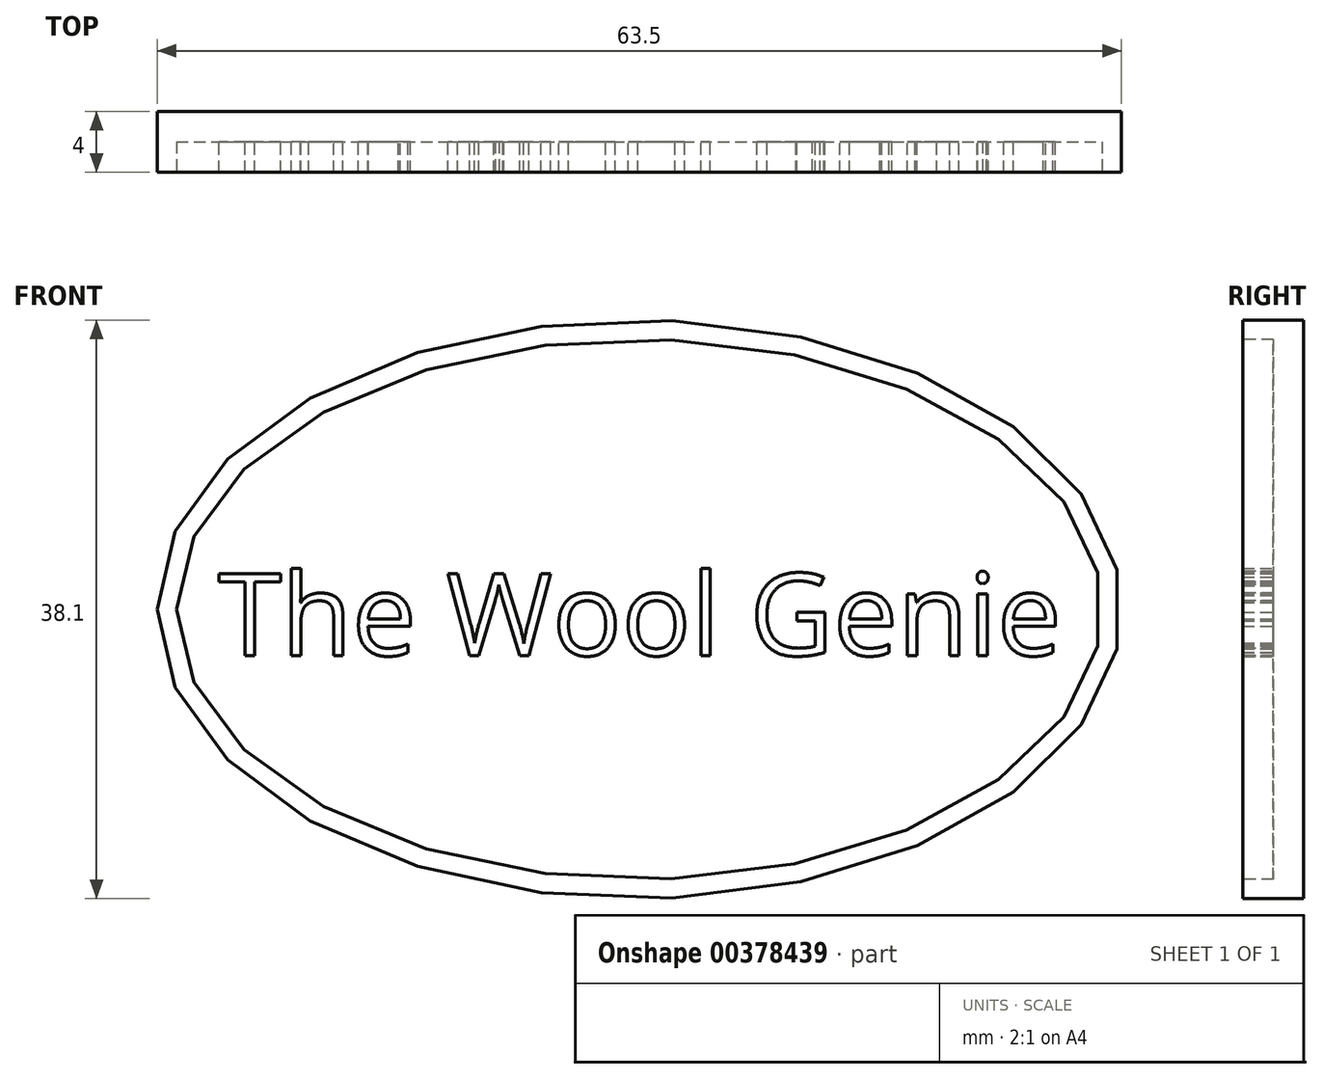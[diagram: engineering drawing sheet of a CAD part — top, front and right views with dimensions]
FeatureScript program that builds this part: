
annotation { "Feature Type Name" : "Feature", "Feature Type Description" : "" }
export const myFeature = defineFeature(function(context is Context, id is Id, definition is map)
    precondition{}
    {
        {
            var Q0;
            Q0=qCreatedBy(makeId("Front.planeOp"),FACE);
            var sketch = newSketch(context, id + "F0", { "sketchPlane" : qUnion([Q0])});
            skEllipse(sketch, "E0", {"center": v(0, 0) * mm, "majorRadius": 31.75 * mm, "minorRadius": 19.05 * mm, "majorAxis": v(-1, 0)});
            skSolve(sketch);
        }
        {
            var Q0;
            Q0=makeQuery(id+"F0.imprint","IMPRINT",FACE,{"disambiguationData":[TD([[makeQuery(id+"F0.imprint","IMPRINT",EDGE,{"derivedFrom":sQuery(id+"F0.wireOp",EDGE,"E0")}),1.0]])]});
            extrude(context, id + "F1", {"entities" : qUnion([Q0]), "depth" : 4 * mm});
        }
        {
            var Q0;
            Q0=makeQuery(id+"F1.opExtrude","CAP_FACE",FACE,{"disambiguationData":[OSD([sQuery(id+"F0.wireOp",EDGE,"E0")])],"isStart":false});
            var sketch = newSketch(context, id + "F2", { "sketchPlane" : qUnion([Q0])});
            skEllipse(sketch, "E1", {"center": v(0, 0) * mm, "majorRadius": 30.48 * mm, "minorRadius": 17.78 * mm, "majorAxis": v(-1, 0)});
            skSolve(sketch);
        }
        {
            var Q0;
            Q0=makeQuery(id+"F2.imprint","IMPRINT",FACE,{"disambiguationData":[TD([[makeQuery(id+"F2.imprint","IMPRINT",EDGE,{"derivedFrom":sQuery(id+"F2.wireOp",EDGE,"E1")}),1.0]])]});
            extrude(context, id + "F3", {"entities" : qUnion([Q0]), "operationType" : NewBodyOperationType.REMOVE, "oppositeDirection" : true, "depth" : 2 * mm});
        }
        {
            var Q0;
            Q0=makeQuery(id+"F3.boolean.opBoolean","COPY",FACE,{"derivedFrom":makeQuery(id+"F3.opExtrude","CAP_FACE",FACE,{"disambiguationData":[OSD([sQuery(id+"F2.wireOp",EDGE,"E1")])],"isStart":false})});
            var sketch = newSketch(context, id + "F4", { "sketchPlane" : qUnion([Q0])});
            skText(sketch, "E2", { "text": "The Wool Genie", "fontName": "OpenSans-Regular.ttf"});
            const initialGuessF4  = {"E2": [-0.02774, -0.00303, 1, 0, 0.00544]};
            skSetInitialGuess(sketch, initialGuessF4);
            skSolve(sketch);
        }
        {
            var Q0;
            Q0 = qSketchRegion(id + "F4", true);
            extrude(context, id + "F5", {"entities" : qUnion([Q0]), "operationType" : NewBodyOperationType.ADD, "depth" : 2 * mm});
        }
    });
